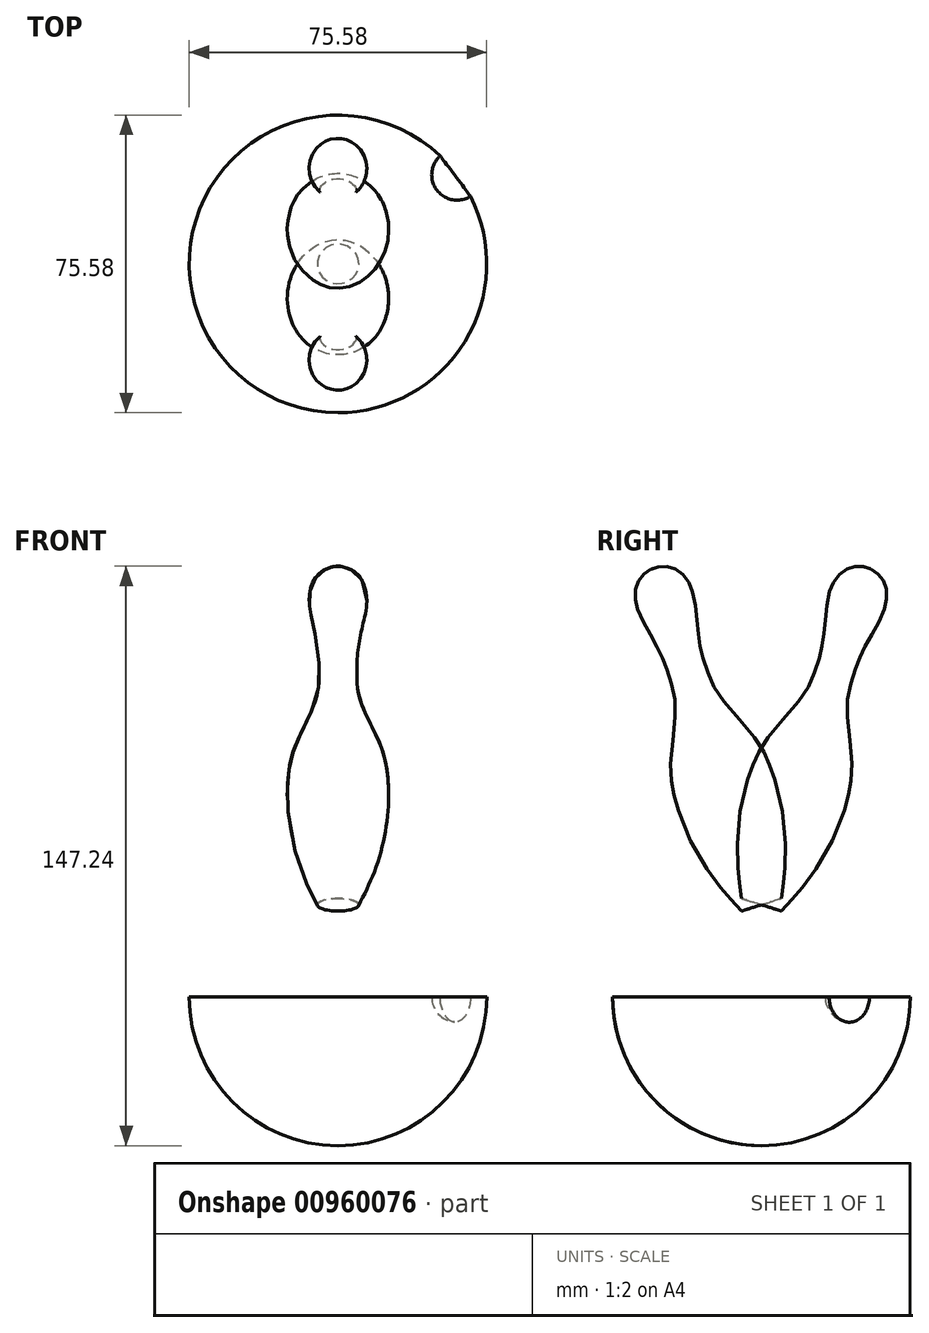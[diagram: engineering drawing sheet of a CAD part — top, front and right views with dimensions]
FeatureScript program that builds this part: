
annotation { "Feature Type Name" : "Feature", "Feature Type Description" : "" }
export const myFeature = defineFeature(function(context is Context, id is Id, definition is map)
    precondition{}
    {
        {
            var Q0;
            Q0=qCreatedBy(makeId("Front.planeOp"),FACE);
            var sketch = newSketch(context, id + "F0", { "sketchPlane" : qUnion([Q0])});
            skLineSegment(sketch, "E0", {"start": v(14, 35.77) * mm, "end": v(14, 0) * mm, "construction": true});
            skLineSegment(sketch, "E1", {"start": v(0, 0) * mm, "end": v(5.29, 0) * mm});
            skLineSegment(sketch, "E2", {"start": v(0, 89.74) * mm, "end": v(0, 0) * mm});
            skFitSpline(sketch, "E3", {"points": [v(1, 89.74) * mm, v(5.51, 87.23) * mm, v(7.32, 80.47) * mm, v(6.57, 75.86) * mm, v(5, 67.4) * mm, v(4.79, 62.06) * mm, v(5.62, 54.63) * mm, v(10.78, 42.26) * mm, v(12.63, 34.19) * mm, v(12.63, 23.93) * mm, v(9.79, 10.57) * mm, v(5.29, 0) * mm], "startDerivative": vector(40.92, 0) * mm, "endDerivative": vector(-45.36, -94.74) * mm});
            skLineSegment(sketch, "E4", {"start": v(1, 89.74) * mm, "end": v(0, 89.74) * mm});
            skPoint(sketch, "E5.orphan", {"position": v(0, 91.3) * mm});
            skSolve(sketch);
        }
        {
            var Q0;
            Q0=makeQuery(id+"F0.imprint","IMPRINT",FACE,{"disambiguationData":[TD([[makeQuery(id+"F0.imprint","IMPRINT",EDGE,{"derivedFrom":sQuery(id+"F0.wireOp",EDGE,"E1")}),1.0]])]});
            var Q1;
            Q1=sQuery(id+"F0.wireOp",EDGE,"E2");
            revolve(context, id + "F1", {"entities" : qUnion([Q0]), "axis" : qUnion([Q1]), "revolveType" : RevolveType.FULL});
        }
        {
            var Q0;
            Q0=makeQuery(id+"F1.opRevolve","SWEPT_FACE",FACE,{"disambiguationData":[OSD([sQuery(id+"F0.wireOp",EDGE,"E1")])]});
            var sketch = newSketch(context, id + "F2", { "sketchPlane" : qUnion([Q0])});
            skLineSegment(sketch, "E6", {"start": v(5.29, 0) * mm, "end": v(-5.29, 0) * mm, "construction": true});
            skSolve(sketch);
        }
        {
            var Q0;
            Q0=makeQuery(id+"F1.opRevolve","SWEPT_BODY",BODY,{"disambiguationData":[OSD([sQuery(id+"F0.wireOp",EDGE,"E1"),sQuery(id+"F0.wireOp",EDGE,"E2"),sQuery(id+"F0.wireOp",EDGE,"E3"),sQuery(id+"F0.wireOp",EDGE,"E4")])]});
            var Q1;
            Q1=sQuery(id+"F2.wireOp",EDGE,"E6");
            transform(context, id + "F3", {"entities" : qUnion([Q0]), "transformType" : TransformType.ROTATION, "transformAxis" : qUnion([Q1]), "angle" : 35 * degree, "makeCopy" : true});
        }
        {
            var Q0;
            Q0=makeQuery(id+"F1.opRevolve","SWEPT_BODY",BODY,{"disambiguationData":[OSD([sQuery(id+"F0.wireOp",EDGE,"E1"),sQuery(id+"F0.wireOp",EDGE,"E2"),sQuery(id+"F0.wireOp",EDGE,"E3"),sQuery(id+"F0.wireOp",EDGE,"E4")])]});
            var Q1;
            Q1=makeQuery(id+"F3.opPattern","COPY",BODY,{"derivedFrom":makeQuery(id+"F1.opRevolve","SWEPT_BODY",BODY,{"disambiguationData":[OSD([sQuery(id+"F0.wireOp",EDGE,"E1"),sQuery(id+"F0.wireOp",EDGE,"E2"),sQuery(id+"F0.wireOp",EDGE,"E3"),sQuery(id+"F0.wireOp",EDGE,"E4")])]}),"instanceName":"1"});
            var Q2;
            Q2=sQuery(id+"F2.wireOp",EDGE,"E6");
            transform(context, id + "F4", {"entities" : qUnion([Q0, Q1]), "transformType" : TransformType.ROTATION, "transformAxis" : qUnion([Q2]), "angle" : 17.56 * degree, "oppositeDirection" : true, "makeCopy" : false});
        }
        {
            var Q0;
            Q0=qCreatedBy(makeId("Right.planeOp"),FACE);
            var sketch = newSketch(context, id + "F5", { "sketchPlane" : qUnion([Q0])});
            skCircle(sketch, "E7", {"center": v(0, -23.4) * mm, "radius": 37.8 * mm});
            skLineSegment(sketch, "E8", {"start": v(0, 14.39) * mm, "end": v(0, -61.2) * mm});
            skLineSegment(sketch, "E9", {"start": v(37.8, -23.4) * mm, "end": v(-37.8, -23.4) * mm});
            skSolve(sketch);
        }
        {
            var Q0;
            {var subQ0=sQuery(id+"F5.wireOp",EDGE,"E8");var subQ1=sQuery(id+"F5.wireOp",EDGE,"E7");var subQ2=makeQuery(id+"F5.imprint","INTERSECT",VERTEX,{"disambiguationData":[OD(0.0)],"derivedFrom":[subQ1,subQ0]});Q0=makeQuery(id+"F5.imprint","IMPRINT",FACE,{"disambiguationData":[TD([[makeQuery(id+"F5.imprint","IMPRINT",EDGE,{"disambiguationData":[TD([[subQ2,1.0]])],"derivedFrom":subQ1}),1.0]])]});}
            var Q1;
            Q1=sQuery(id+"F5.wireOp",EDGE,"E8");
            revolve(context, id + "F6", {"surfaceOperationType" : NewSurfaceOperationType.NEW, "entities" : qUnion([Q0]), "axis" : qUnion([Q1]), "revolveType" : RevolveType.FULL});
        }
        {
            var Q0;
            Q0=qCreatedBy(makeId("Top.planeOp"),FACE);
            var sketch = newSketch(context, id + "F7", { "sketchPlane" : qUnion([Q0])});
            skCircle(sketch, "E10", {"center": v(26.07, -14.11) * mm, "radius": 3.09 * mm});
            skCircle(sketch, "E11", {"center": v(17.42, -24.47) * mm, "radius": 3.09 * mm});
            skLineSegment(sketch, "E12", {"start": v(20.5, -24.58) * mm, "end": v(14.33, -24.58) * mm});
            skLineSegment(sketch, "E13", {"start": v(29.14, -14.44) * mm, "end": v(23.03, -13.55) * mm});
            skSolve(sketch);
        }
        {
            var Q0;
            {var subQ0=sQuery(id+"F7.wireOp",EDGE,"E12");Q0=makeQuery(id+"F7.imprint","IMPRINT",FACE,{"disambiguationData":[TD([[makeQuery(id+"F7.imprint","IMPRINT",EDGE,{"derivedFrom":subQ0}),1.0]])]});}
            var Q1;
            Q1=sQuery(id+"F7.wireOp",EDGE,"E12");
            revolve(context, id + "F8", {"operationType" : NewBodyOperationType.REMOVE, "surfaceOperationType" : NewSurfaceOperationType.NEW, "entities" : qUnion([Q0]), "axis" : qUnion([Q1]), "revolveType" : RevolveType.FULL, "oppositeDirection" : true});
        }
        {
            var Q0;
            {var subQ0=sQuery(id+"F7.wireOp",EDGE,"E13");Q0=makeQuery(id+"F7.imprint","IMPRINT",FACE,{"disambiguationData":[TD([[makeQuery(id+"F7.imprint","IMPRINT",EDGE,{"derivedFrom":subQ0}),1.0]])]});}
            var Q1;
            Q1=sQuery(id+"F7.wireOp",EDGE,"E13");
            revolve(context, id + "F9", {"operationType" : NewBodyOperationType.REMOVE, "surfaceOperationType" : NewSurfaceOperationType.NEW, "entities" : qUnion([Q0]), "axis" : qUnion([Q1]), "revolveType" : RevolveType.FULL, "oppositeDirection" : true});
        }
        {
            var Q0;
            Q0=makeQuery(id+"F6.opRevolve","SWEPT_FACE",FACE,{"disambiguationData":[OSD([sQuery(id+"F5.wireOp",EDGE,"E9")])]});
            var sketch = newSketch(context, id + "F10", { "sketchPlane" : qUnion([Q0])});
            skCircle(sketch, "E14", {"center": v(30.26, 22.65) * mm, "radius": 6.44 * mm});
            skLineSegment(sketch, "E15", {"start": v(36.7, 22.65) * mm, "end": v(23.82, 22.65) * mm});
            skSolve(sketch);
        }
        {
            var Q0;
            {var subQ0=sQuery(id+"F10.wireOp",EDGE,"E15");var subQ1=sQuery(id+"F10.wireOp",EDGE,"E14");var subQ2=makeQuery(id+"F10.imprint","INTERSECT",VERTEX,{"disambiguationData":[OD(1.0)],"derivedFrom":[subQ1,subQ0]});Q0=makeQuery(id+"F10.imprint","IMPRINT",FACE,{"disambiguationData":[TD([[makeQuery(id+"F10.imprint","IMPRINT",EDGE,{"disambiguationData":[TD([[subQ2,1.0]])],"derivedFrom":subQ1}),1.0]])]});}
            var Q1;
            {var subQ0=sQuery(id+"F10.wireOp",EDGE,"E15");var subQ1=sQuery(id+"F10.wireOp",EDGE,"E14");var subQ2=makeQuery(id+"F10.imprint","INTERSECT",VERTEX,{"disambiguationData":[OD(0.0)],"derivedFrom":[subQ1,subQ0]});Q1=makeQuery(id+"F10.imprint","IMPRINT",FACE,{"disambiguationData":[TD([[makeQuery(id+"F10.imprint","IMPRINT",EDGE,{"disambiguationData":[TD([[subQ2,-1.0]])],"derivedFrom":subQ1}),1.0]])]});}
            var Q2;
            Q2=sQuery(id+"F10.wireOp",EDGE,"E15");
            revolve(context, id + "F11", {"operationType" : NewBodyOperationType.REMOVE, "surfaceOperationType" : NewSurfaceOperationType.NEW, "entities" : qUnion([Q0, Q1]), "axis" : qUnion([Q2]), "revolveType" : RevolveType.FULL, "oppositeDirection" : true});
        }
    });
